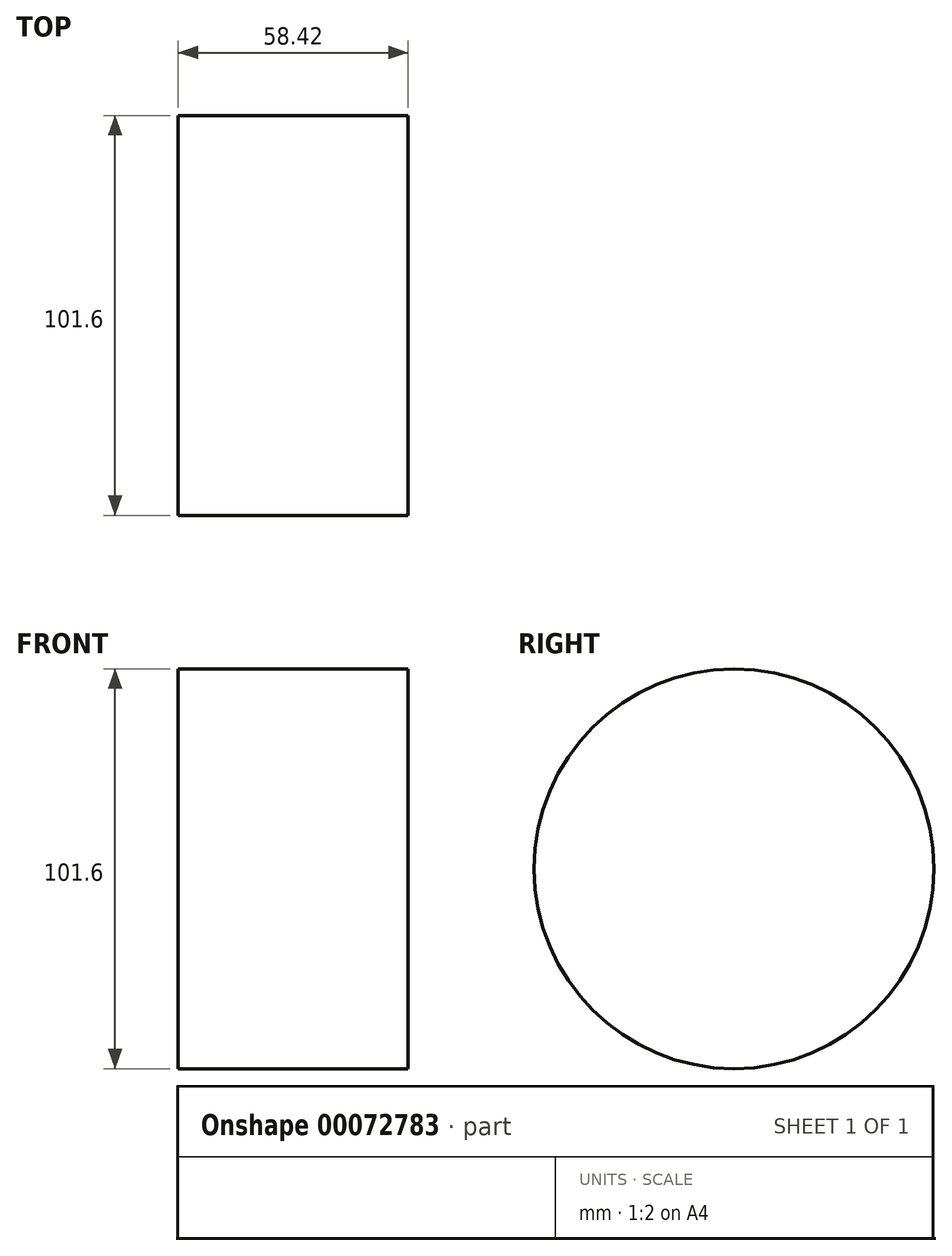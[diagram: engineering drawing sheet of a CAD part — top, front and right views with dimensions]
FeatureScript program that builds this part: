
annotation { "Feature Type Name" : "Feature", "Feature Type Description" : "" }
export const myFeature = defineFeature(function(context is Context, id is Id, definition is map)
    precondition{}
    {
        {
            var Q0;
            Q0=qCreatedBy(makeId("Right.planeOp"),FACE);
            var sketch = newSketch(context, id + "F0", { "sketchPlane" : qUnion([Q0])});
            skCircle(sketch, "E0", {"center": v(200.63, 0) * mm, "radius": 50.8 * mm});
            skCircle(sketch, "E1", {"center": v(0, 0) * mm, "radius": 50.8 * mm});
            skSolve(sketch);
        }
        {
            var Q0;
            Q0=qCreatedBy(makeId("Right.planeOp"),FACE);
            var sketch = newSketch(context, id + "F1", { "sketchPlane" : qUnion([Q0])});
            skArc(sketch, "E2", {"start": v(-60.76, 152.4) * mm, "mid": v(-90.36, 78.77) * mm, "end": v(-99.95, 0) * mm});
            skCircle(sketch, "E3", {"center": v(24.14, -27.84) * mm, "radius": 127 * mm});
            skLineSegment(sketch, "E4", {"start": v(172.1, -57.2) * mm, "end": v(89.3, -143.3) * mm});
            skSolve(sketch);
        }
        {
            var Q0;
            Q0=makeQuery(id+"F0.imprint","IMPRINT",FACE,{"disambiguationData":[TD([[makeQuery(id+"F0.imprint","IMPRINT",EDGE,{"derivedFrom":sQuery(id+"F0.wireOp",EDGE,"E0")}),1.0]])]});
            extrude(context, id + "F2", {"entities" : qUnion([Q0]), "endBound" : BoundingType.SYMMETRIC, "depth" : 58.42 * mm});
        }
    });
